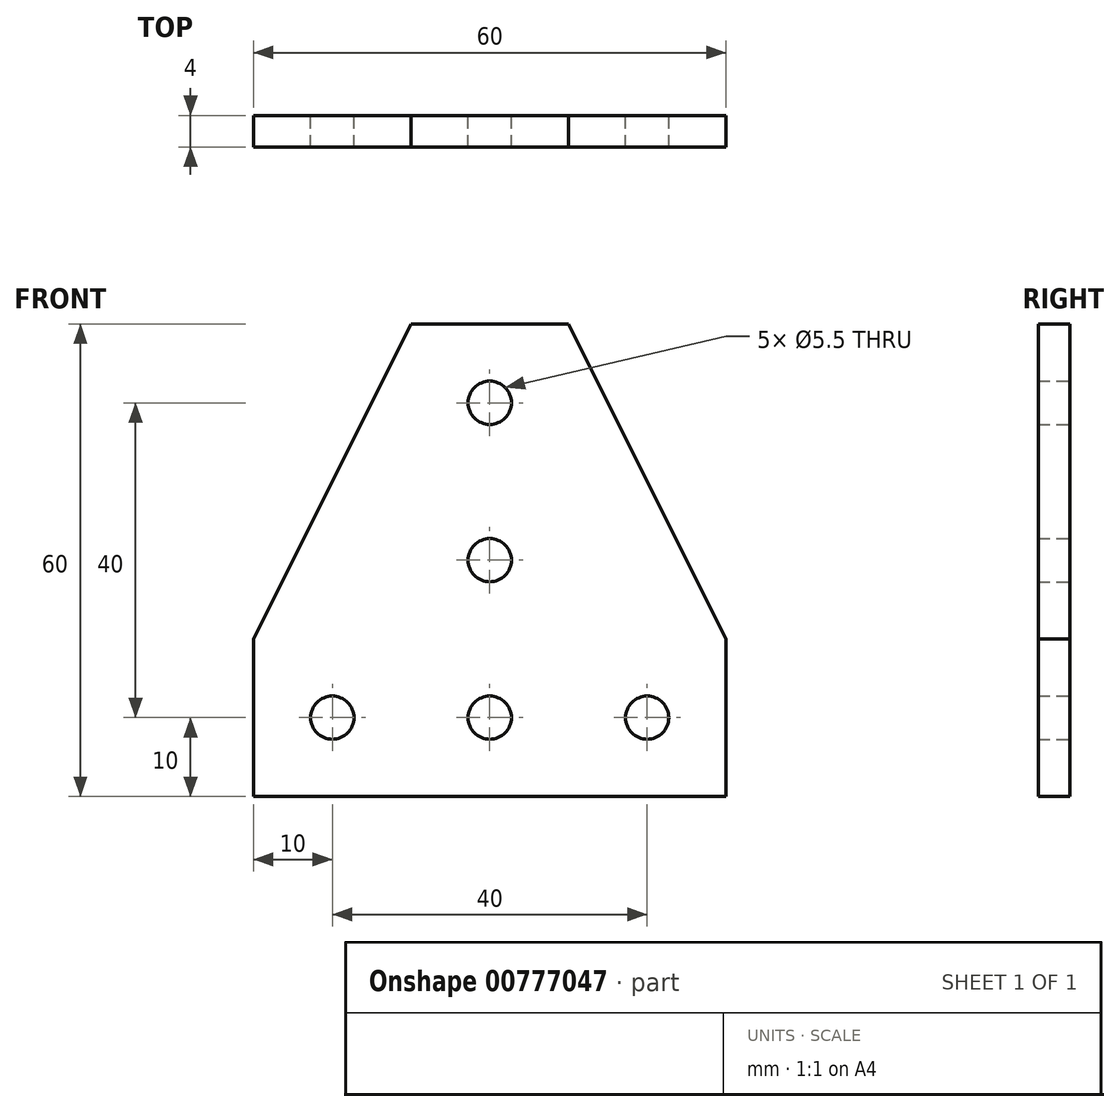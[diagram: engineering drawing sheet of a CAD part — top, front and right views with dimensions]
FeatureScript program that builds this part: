
annotation { "Feature Type Name" : "Feature", "Feature Type Description" : "" }
export const myFeature = defineFeature(function(context is Context, id is Id, definition is map)
    precondition{}
    {
        {
            var Q0;
            Q0=qCreatedBy(makeId("Front.planeOp"),FACE);
            var sketch = newSketch(context, id + "F0", { "sketchPlane" : qUnion([Q0])});
            skLineSegment(sketch, "E0", {"start": v(-30, -30) * mm, "end": v(30, -30) * mm});
            skLineSegment(sketch, "E1", {"start": v(30, -30) * mm, "end": v(30, -10) * mm});
            skCircle(sketch, "E2", {"center": v(-20, -20) * mm, "radius": 2.75 * mm});
            skPoint(sketch, "E2.centerSnap0", {"position": v(30, -20) * mm});
            skCircle(sketch, "E3", {"center": v(0, -20) * mm, "radius": 2.75 * mm});
            skCircle(sketch, "E4", {"center": v(20, -20) * mm, "radius": 2.75 * mm});
            skLineSegment(sketch, "E5", {"start": v(-10, 30) * mm, "end": v(10, 30) * mm});
            skLineSegment(sketch, "E6", {"start": v(-30, -30) * mm, "end": v(-30, -10) * mm});
            skLineSegment(sketch, "E7", {"start": v(-30, -10) * mm, "end": v(-10, 30) * mm});
            skLineSegment(sketch, "E8", {"start": v(10, 30) * mm, "end": v(30, -10) * mm});
            skCircle(sketch, "E9", {"center": v(0, 0) * mm, "radius": 2.75 * mm});
            skCircle(sketch, "E10", {"center": v(0, 20) * mm, "radius": 2.75 * mm});
            skSolve(sketch);
        }
        {
            var Q0;
            Q0=qSketchRegion(id+"F0",true);
            extrude(context, id + "F1", {"entities" : qUnion([Q0]), "depth" : 4 * mm});
        }
    });
